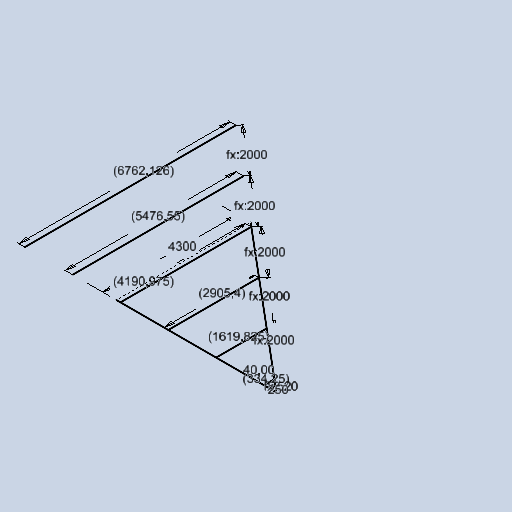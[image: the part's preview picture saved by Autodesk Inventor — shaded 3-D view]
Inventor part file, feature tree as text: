
AUTODESK INVENTOR PART (.ipt)
format: ipt  version: 2025 (Build 290162010, 162A)  size: 109,056 bytes
history: native  units: mm
features: sketch x1
ambient origin geometry x8: Origin, YZ Plane, XZ Plane, XY Plane, X Axis, Y Axis, Z Axis, Center Point
feature tree (1):
  sketch  "Sketch2"  dims[d2=6.981317mm d3=4300.0mm d6=334.249557mm d7=250.0mm d8=520.0mm d12=1837.151267mm d13=2905.399996mm d14=5476.550435mm d15=6762.125654mm d16=2000.0mm d17=2000.0mm d18=2000.0mm d19=2000.0mm d20=2000.0mm d21=1619.824776mm d22=4190.975215mm]
